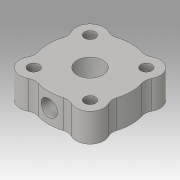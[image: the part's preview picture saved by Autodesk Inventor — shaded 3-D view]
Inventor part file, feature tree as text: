
AUTODESK INVENTOR PART (.ipt)
format: ipt  version: 2016 (Build 200138000, 138)  size: 146,432 bytes
history: native  units: in
note: dims shown in document units (in); Inventor stores cm internally (conversion verified against a paired STEP export)
features: fillet x1
ambient origin geometry x8: Origin, YZ Plane, XZ Plane, XY Plane, X Axis, Y Axis, Z Axis, Center Point
bodies: Solid1 (feature_tree)
feature tree (1):
  fillet  "Fillet1"  [1 undecoded]
note: 1 required parameter value undecoded (feature->parameter linkage not recoverable at this tier; creation-order binding heuristic only, values carry confidence <= 0.55)
